# Revit family: Wicline_95_Open_in_standard_single_casement
name_source: partatom
category: Windows
revit_build: Autodesk Revit Architecture 2014 (Build: 20130308_1515(x64)
units: mm (PartAtom-declared; Revit-internal decimal feet)

## types (1)
- Wicline_95_Open_in_standard_single_casement
    Acoustic = Rw (C;Ctr) = 47 (-1;-4) dB
    Air Permeability = Class 5
    Analytic Construction = <None>
    Date of publishing = 3/14/2015
    Default Sill Height = 800 mm  [stored 2.62467 ft]
    Description = The WICLINE 95 window system meets the highest energy efficiency standards with a frame depth of only 95 mm and a slim sightline of only 125 mm. The Thermo Frame insulation zone for WICLINE 95 is located inside the rebate area of the window and can be fabricated and installed quickly and easily through an intelligent clamping system. This feature allows adjustment of the Uf-value as required for the building. The main components of the WICLINE 65 and 75 series are used for WICLINE 95 in line with the WICONA Unysis principle to simplify ordering and minimize stock keeping. The new ETC Intelligence® thermal break zone through its intelligent material mix achieves passive house class phB and removes the need for foam inserts in the sash or frame profile.
    Design country = Germany
    Edition number = 1
    Frame 1019004 = Yes
    Frame 1019006 = No
    Frame 1019010 = No
    Frame Material = WICONA - Aluminium - RAL7016 - Anthracite Grey - Matt
    Frame Thickness = 95 mm  [stored 0.31168 ft]
    Frame Width = 65 mm  [stored 0.213255 ft]
    Frame Width 2 = 40 mm  [stored 0.131234 ft]
    Glass Material = WICONA -  Glass
    Handle Material = Aluminium
    Height = 1500 mm  [stored 4.92126 ft]
    Leaf Height = 1420 mm
    Leaf Material = WICONA - Aluminium - RAL7016 - Anthracite Grey - Matt
    Leaf Width = 920 mm
    Manufacturer = Wicona
    Manufacturer country = Germany
    Manufacturer name = Wicona
    Material main = Aluminium
    Material secondary = Glass
    Maximum Sash Weight = 150kg as standard design, heavier weights can easily be customised
    Mechanical Strength = Class 4
    Model = Wicline 95
    Nominal height = 150000
    Nominal width = 100000
    Operating Forces = Class 1
    Product Guid = e95bb49c-67c8-4fe8-88fb-b6bba030be1f
    Product SKU = WICLINE_95_W
    Product data url = http://bimobject.com
    Product family = Windows & Doors
    Product group = Windows
    QR code = http://bimobject.com
    Quality Assurance = Certified according to ISO 9001:2008
    Repeated Opening/Closing = Class 3 (20,000 cycles)
    Resistance to wind load = Class C5/B5
    Sash 1019110 = No
    Sash 1019111 = No
    Sash 1019112 = Yes
    URL = http://www.wicona.com
    Wall Closure = By host
    Watertightness = E900
    Weight Net (Kg) = 0
    Width = 1000 mm  [stored 3.28084 ft]
    Window Offset = 60 mm  [stored 0.19685 ft]

note: [stored X ft] marks values corroborated as IEEE doubles in the binary element streams (Revit-internal decimal feet)

## geometry (parser evidence)
native form markers: Blend x4, Sweep x12
no freeform markers — native parametric forms only
